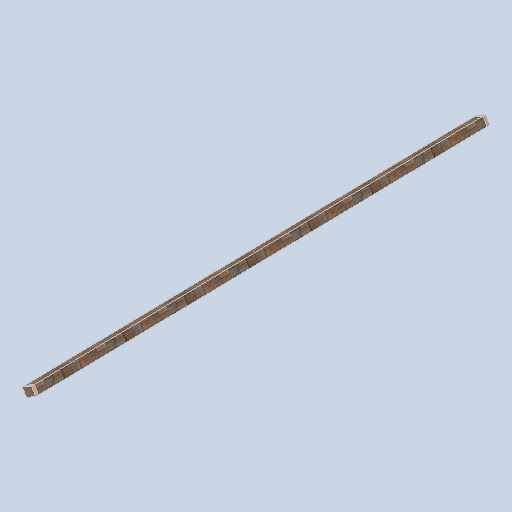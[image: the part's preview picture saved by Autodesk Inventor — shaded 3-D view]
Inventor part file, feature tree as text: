
AUTODESK INVENTOR PART (.ipt)
format: ipt  version: 2024.2 (Build 282272000, 272)  size: 136,192 bytes
history: native  units: in
note: dims shown in document units (in); Inventor stores cm internally (conversion verified against a paired STEP export)
features: sketch x4, other x3, plane x2
ambient origin geometry x8: Origin, YZ Plane, XZ Plane, XY Plane, X Axis, Y Axis, Z Axis, Center Point
bodies: Solid1 (feature_tree)
feature tree (9):
  other  "support_beam_segment_0105.ipt"
  other  "Solid1::support_beam_segment_0105.ipt"
  other  "TaggingFeature1"
  sketch  "Sketch1"  dims[d0=0.3937in]
  sketch  "Sketch2"
  sketch  "Sketch3"
  sketch  "Sketch4"
  plane  "Work Plane1"
  plane  "Work Plane2"
